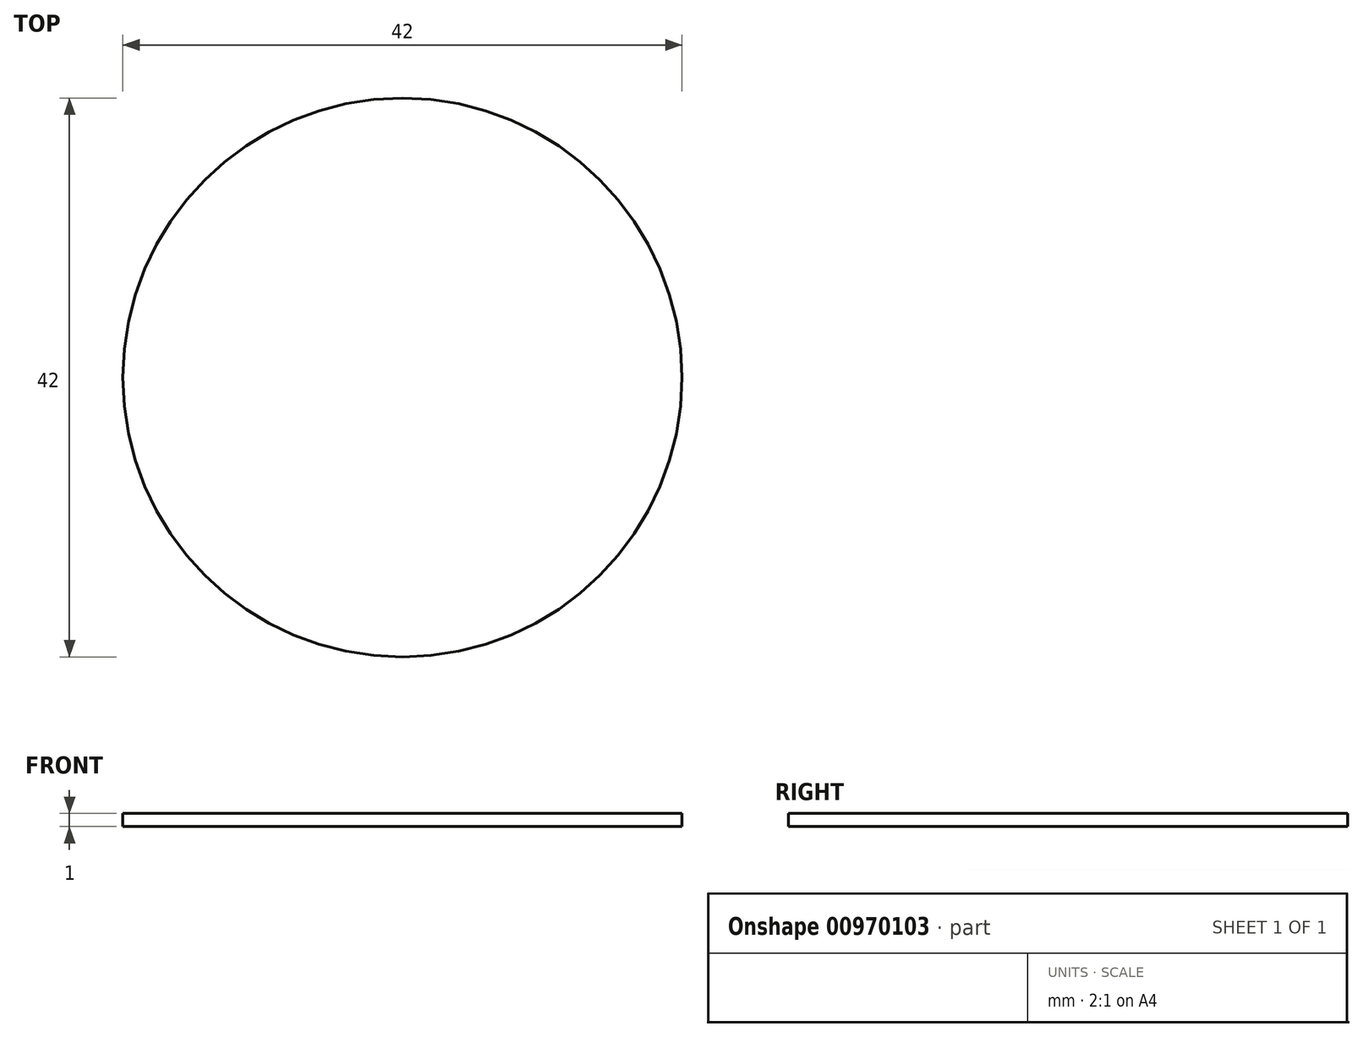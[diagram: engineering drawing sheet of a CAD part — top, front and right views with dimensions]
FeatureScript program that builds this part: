
annotation { "Feature Type Name" : "Feature", "Feature Type Description" : "" }
export const myFeature = defineFeature(function(context is Context, id is Id, definition is map)
    precondition{}
    {
        {
            var Q0;
            Q0=qCreatedBy(makeId("Top.planeOp"),FACE);
            var sketch = newSketch(context, id + "F0", { "sketchPlane" : qUnion([Q0])});
            skCircle(sketch, "E0", {"center": v(0, 0) * mm, "radius": 21 * mm});
            skSolve(sketch);
        }
        {
            var Q0;
            Q0=makeQuery(id+"F0.imprint","IMPRINT",FACE,{"disambiguationData":[TD([[makeQuery(id+"F0.imprint","IMPRINT",EDGE,{"derivedFrom":sQuery(id+"F0.wireOp",EDGE,"E0")}),1.0]])]});
            extrude(context, id + "F1", {"entities" : qUnion([Q0]), "depth" : 1 * mm, "offsetDistance" : 25 * mm});
        }
    });
